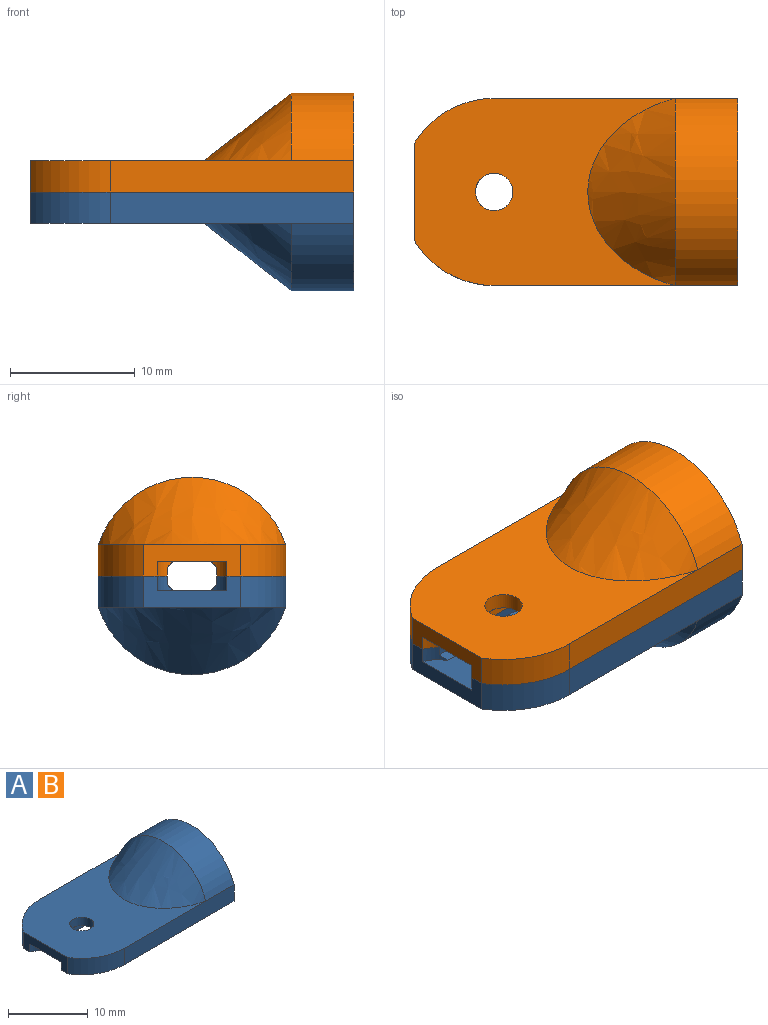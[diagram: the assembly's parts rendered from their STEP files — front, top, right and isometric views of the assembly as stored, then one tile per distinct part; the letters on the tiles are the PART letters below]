
ASSEMBLY  parts=2 mates=1
PART A: 24 faces, bbox 25.9x15x14.1 mm
  f0: plane 25.9x5.5mm, normal (0,0,-1), area 101.6mm2, adj f3,f5,f7,f9,f13,f15,f22,f23
  f1: cylinder r=7.5mm len=6.4mm, axis (0,0,-1), area 19.2mm2, adj f2,f10,f11,f23
  f2: plane 25.9x5.5mm, normal (0,0,-1), area 101.6mm2, adj f1,f4,f7,f10,f13,f15,f21,f23
  f3: cylinder r=7.5mm len=6.4mm, axis (0,0,-1), area 19.2mm2, adj f0,f9,f11,f23
  f4: plane 16.76x0.7mm, normal (0,1,0), area 11.7mm2, adj f2,f7,f20,f21
  f5: plane 16.76x0.7mm, normal (0,-1,0), area 11.7mm2, adj f0,f7,f17,f22
  f6: cylinder r=1.5mm len=3mm, axis (0,0,-1), area 12.3mm2, adj f11,f18,f19
  f7: plane 12.4x2.5mm, normal (1,0,0), area 25.6mm2, adj f0,f2,f4,f5,f13,f16,f17,f19
  f8: plane 11.35x3.7mm, normal (1,0,0), area 30.2mm2, adj f13,f16
  f9: plane 19.5x2.5mm, normal (0,1,0), area 48.8mm2, adj f0,f3,f11,f14,f15
  f10: plane 19.5x2.5mm, normal (0,-1,0), area 48.8mm2, adj f1,f2,f11,f14,f15
  f11: plane 20.9x15mm, normal (0,0,1), area 216.2mm2, adj f1,f3,f6,f9,f10,f12,f23
  f12: bspline ~15x14.12mm, area 107.8mm2, adj f11,f14
  f13: cylinder r=6.2mm len=12.4mm, axis (-1,0,0), area 112.8mm2, adj f0,f2,f7,f8,f15,f16
  f14: cylinder r=7.91mm len=15mm, axis (-1,0,0), area 98.7mm2, adj f9,f10,f12,f15
  f15: plane 15x7.91mm, normal (1,0,0), area 36.4mm2, adj f0,f2,f9,f10,f13,f14
  f16: plane 11.35x3mm, normal (0,0,-1), area 34mm2, adj f7,f8,f13
  f17: plane 16.78x0.52mm, normal (0,-0.71,-0.71), area 11.7mm2, adj f5,f7,f18,f19,f22
  f18: plane 6.4x5.58mm, normal (0,0,-1), area 18mm2, adj f6,f17,f20,f21,f22,f23
  f19: plane 11.5x3mm, normal (0,0,-1), area 31mm2, adj f6,f7,f17,f20
  f20: plane 16.78x0.52mm, normal (0,0.71,-0.71), area 11.7mm2, adj f4,f7,f18,f19,f21
  f21: cylinder r=3mm len=1.5mm, axis (0,0,-1), area 1.8mm2, adj f2,f4,f18,f20,f23
  f22: cylinder r=3mm len=1.5mm, axis (0,0,-1), area 1.8mm2, adj f0,f5,f17,f18,f23
  f23: plane 7.82x2.5mm, normal (-1,0,0), area 12.9mm2, adj f0,f1,f2,f3,f11,f18,f21,f22
PART B: same geometry as A
PLACE A rot(axis=(1,0,0),180deg) t=(0,0,0)mm
PLACE B at identity
MATE fastened A.f1 <-> B.f1  axis (0,0,1) through (0,0,0)mm
